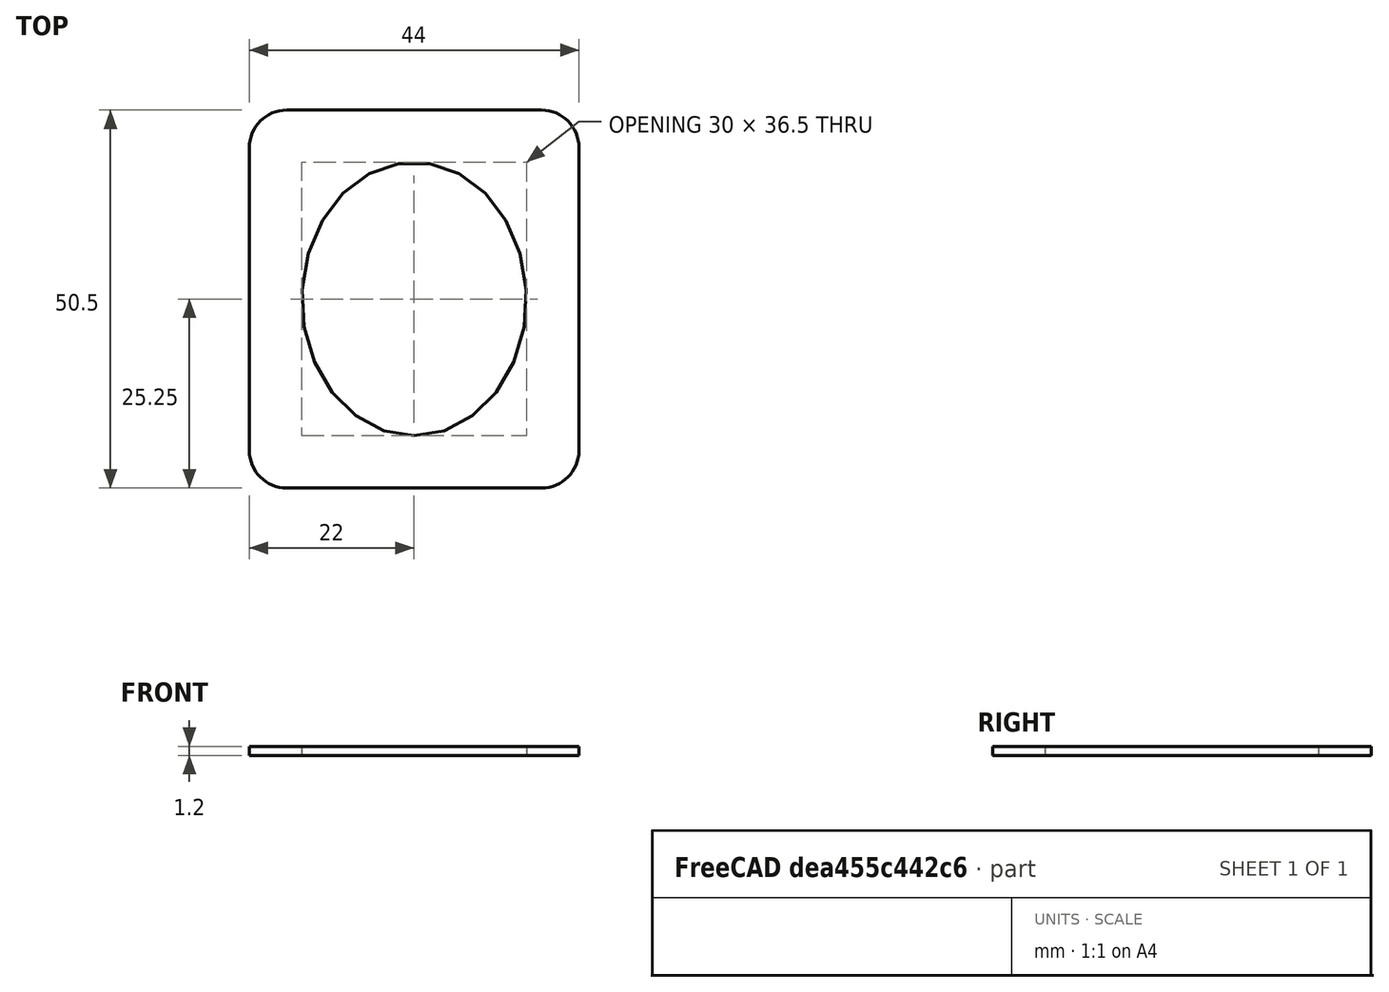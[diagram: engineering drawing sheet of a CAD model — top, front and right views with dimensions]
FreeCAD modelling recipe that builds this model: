
FCSTD DOCUMENT  (FreeCAD 0.17R13528 (Git))
Label: tbstand
License: All rights reserved
LicenseURL: http://en.wikipedia.org/wiki/All_rights_reserved
objects: Sketcher::SketchObject×1, PartDesign::Pad×1, PartDesign::Body×1
note: 4 computed .brp shape members not serialized (recipe doc carries the construction recipe); baked Part::Feature solids carry a one-line shape summary decoded from their .brp

FEATURE [Sketcher::SketchObject] Sketch
  MapMode = 5
  Support = -> [XY_Plane]
  expr: Constraints[26] = Constraints.Height + 14mm
  expr: Constraints[25] = Constraints.Width + 14mm
  sketch-geometry (13):
    g0: Ellipse CenterX=0 CenterY=0 CenterZ=0 NormalX=0 NormalY=0 NormalZ=1 MajorRadius=18.25 MinorRadius=15 AngleXU=-1.5708
    g1: LineSegment [constr] StartX=0 StartY=-18.25 StartZ=0 EndX=0 EndY=18.25 EndZ=0
    g2: LineSegment [constr] StartX=15 StartY=0 StartZ=0 EndX=-15 EndY=0 EndZ=0
    g3: GeomPoint X=0 Y=-10.3953 Z=0
    g4: GeomPoint X=0 Y=10.3953 Z=0
    g5: LineSegment StartX=-17 StartY=25.25 StartZ=0 EndX=17 EndY=25.25 EndZ=0
    g6: LineSegment StartX=22 StartY=20.25 StartZ=0 EndX=22 EndY=-20.25 EndZ=0
    g7: LineSegment StartX=17 StartY=-25.25 StartZ=0 EndX=-17 EndY=-25.25 EndZ=0
    g8: LineSegment StartX=-22 StartY=-20.25 StartZ=0 EndX=-22 EndY=20.25 EndZ=0
    g9: ArcOfCircle CenterX=-17 CenterY=20.25 CenterZ=0 NormalX=0 NormalY=0 NormalZ=1 AngleXU=0 Radius=5 StartAngle=1.5708 EndAngle=3.14159
    g10: ArcOfCircle CenterX=17 CenterY=20.25 CenterZ=0 NormalX=0 NormalY=0 NormalZ=1 AngleXU=0 Radius=5 StartAngle=0 EndAngle=1.5708
    g11: ArcOfCircle CenterX=17 CenterY=-20.25 CenterZ=0 NormalX=0 NormalY=0 NormalZ=1 AngleXU=0 Radius=5 StartAngle=4.71239 EndAngle=6.28319
    g12: ArcOfCircle CenterX=-17 CenterY=-20.25 CenterZ=0 NormalX=0 NormalY=0 NormalZ=1 AngleXU=0 Radius=5 StartAngle=3.14159 EndAngle=4.71239
  constraints (24):
    c: InternalAlignment(g1-g4 -> g0) x4
    c: Coincident(g0,g-1)
    c: Vertical(g1)
    c: DistanceY(g1,g1) = 36.5  'Height'
    c: DistanceX(g2,g2) = 30  'Width'
    c: Horizontal(g5)
    c: Horizontal(g7)
    c: Vertical(g6)
    c: Vertical(g8)
    c: Tangent(g5,g9) = 1.5708
    c: Tangent(g8,g9) = 1.5708
    c: Tangent(g5,g10) = 1.5708
    c: Tangent(g6,g10) = 1.5708
    c: Tangent(g6,g11) = 1.5708
    c: Tangent(g7,g11) = 1.5708
    c: Tangent(g7,g12) = 1.5708
    c: Tangent(g8,g12) = 1.5708
    c: Equal(g12,g11)
    c: Equal(g11,g10)
    c: Radius(g9) = 5
    c: Symmetric(g8,g6,g-2)
    c: Symmetric(g7,g5,g-1)
    c: DistanceX(g8,g6) = 44
    c: DistanceY(g7,g5) = 50.5
FEATURE [PartDesign::Pad] Pad
  Length = 1.2
  Length2 = 100
  Profile = -> Sketch
  Type = 0
FEATURE [PartDesign::Body] Body
  Group = -> [Sketch,Pad]
  Origin = -> Origin
  Tip = -> Pad
